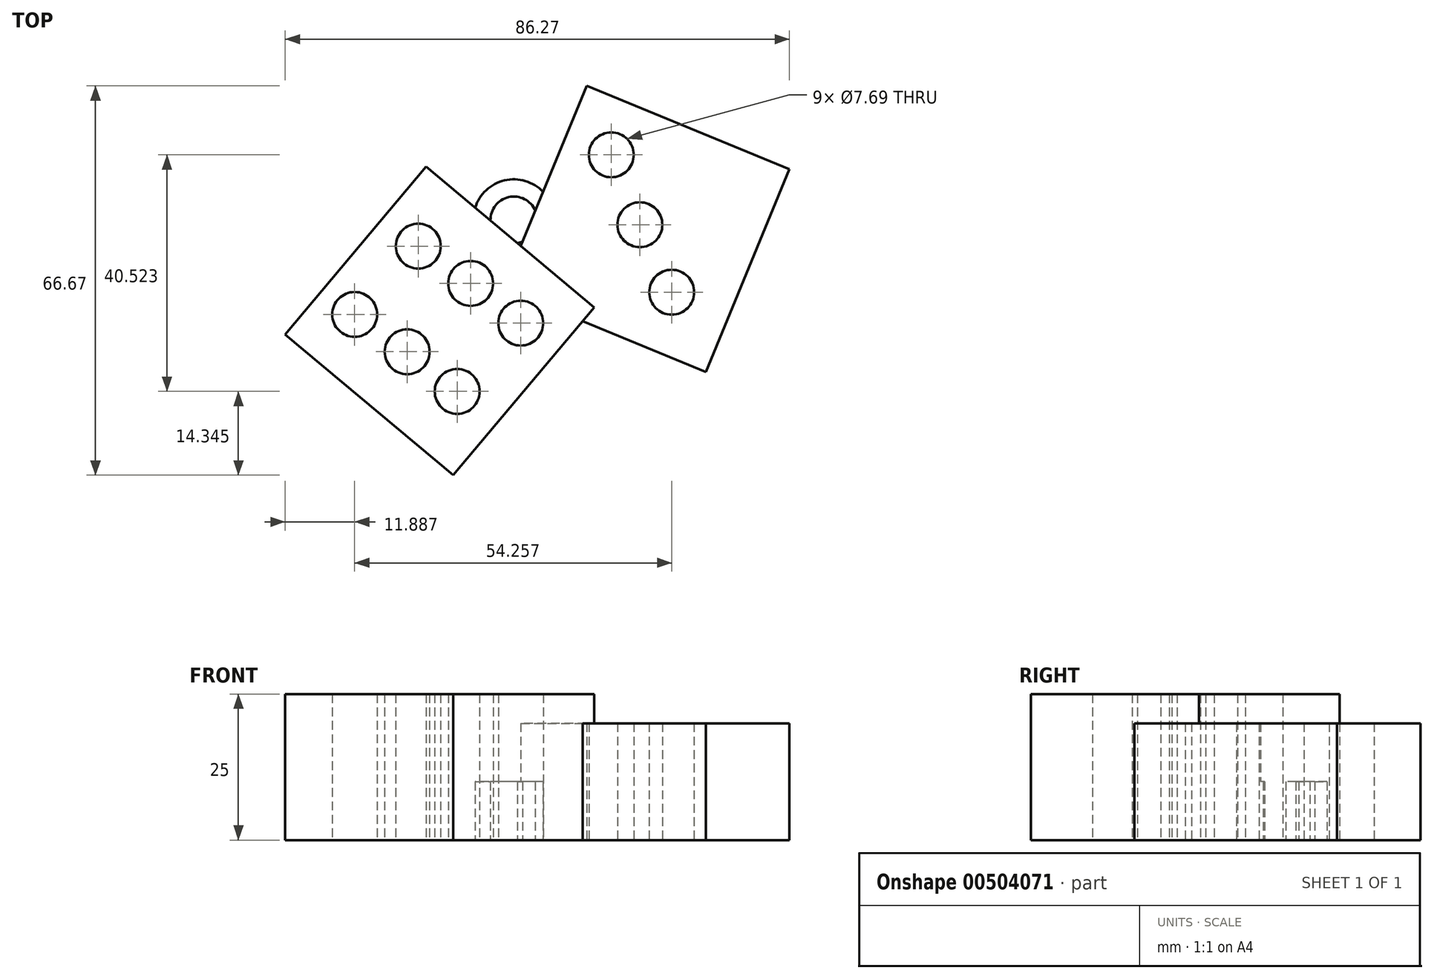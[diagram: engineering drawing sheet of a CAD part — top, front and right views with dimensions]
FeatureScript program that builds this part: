
annotation { "Feature Type Name" : "Feature", "Feature Type Description" : "" }
export const myFeature = defineFeature(function(context is Context, id is Id, definition is map)
    precondition{}
    {
        {
            var Q0;
            Q0=qCreatedBy(makeId("Top.planeOp"),FACE);
            var sketch = newSketch(context, id + "F0", { "sketchPlane" : qUnion([Q0])});
            skLineSegment(sketch, "E0.bottom", {"start": v(-13.76, 11) * mm, "end": v(14.98, -13.11) * mm});
            skLineSegment(sketch, "E0.top", {"start": v(-37.87, -17.74) * mm, "end": v(-9.13, -41.85) * mm});
            skLineSegment(sketch, "E0.left", {"start": v(-13.76, 11) * mm, "end": v(-37.87, -17.74) * mm});
            skLineSegment(sketch, "E0.right", {"start": v(14.98, -13.11) * mm, "end": v(-9.13, -41.85) * mm});
            skLineSegment(sketch, "E1.bottom", {"start": v(13.72, 24.82) * mm, "end": v(48.4, 10.53) * mm});
            skLineSegment(sketch, "E1.top", {"start": v(-0.57, -9.87) * mm, "end": v(34.11, -24.16) * mm});
            skLineSegment(sketch, "E1.left", {"start": v(13.72, 24.82) * mm, "end": v(-0.57, -9.87) * mm});
            skLineSegment(sketch, "E1.right", {"start": v(48.4, 10.53) * mm, "end": v(34.11, -24.16) * mm});
            skSolve(sketch);
        }
        {
            var Q0;
            {var subQ0=sQuery(id+"F0.wireOp",EDGE,"E0.right");var subQ1=sQuery(id+"F0.wireOp",EDGE,"E0.bottom");var subQ2=makeQuery(id+"F0.imprint","INTERSECT",VERTEX,{"derivedFrom":[subQ1,subQ0]});Q0=makeQuery(id+"F0.imprint","IMPRINT",FACE,{"disambiguationData":[TD([[makeQuery(id+"F0.imprint","IMPRINT",EDGE,{"disambiguationData":[TD([[subQ2,1.0]])],"derivedFrom":subQ1}),-1.0]])]});}
            var Q1;
            {var subQ1=sQuery(id+"F0.wireOp",EDGE,"E0.top");Q1=makeQuery(id+"F0.imprint","IMPRINT",FACE,{"disambiguationData":[TD([[makeQuery(id+"F0.imprint","IMPRINT",EDGE,{"derivedFrom":subQ1}),1.0]])]});}
            extrude(context, id + "F1", {"entities" : qUnion([Q0, Q1]), "depth" : 25 * mm});
        }
        {
            var Q0;
            {var subQ6=sQuery(id+"F0.wireOp",EDGE,"E1.bottom");Q0=makeQuery(id+"F0.imprint","IMPRINT",FACE,{"disambiguationData":[TD([[makeQuery(id+"F0.imprint","IMPRINT",EDGE,{"derivedFrom":subQ6}),-1.0]])]});}
            extrude(context, id + "F2", {"entities" : qUnion([Q0]), "operationType" : NewBodyOperationType.ADD, "depth" : 20 * mm});
        }
        {
            var Q0;
            Q0=qCreatedBy(makeId("Top.planeOp"),FACE);
            var sketch = newSketch(context, id + "F3", { "sketchPlane" : qUnion([Q0])});
            skCircle(sketch, "E2", {"center": v(-15.1, -2.62) * mm, "radius": 3.84 * mm});
            skCircle(sketch, "E3.1.0.0", {"center": v(-25.98, -14.32) * mm, "radius": 3.84 * mm});
            skCircle(sketch, "E4", {"center": v(-6.13, -9.01) * mm, "radius": 3.84 * mm});
            skCircle(sketch, "E5.1.0.0", {"center": v(-17, -20.7) * mm, "radius": 3.84 * mm});
            skCircle(sketch, "E6", {"center": v(2.44, -15.81) * mm, "radius": 3.84 * mm});
            skCircle(sketch, "E7.1.0.0", {"center": v(-8.44, -27.5) * mm, "radius": 3.84 * mm});
            skCircle(sketch, "E8", {"center": v(17.94, 13.02) * mm, "radius": 3.84 * mm});
            skCircle(sketch, "E9", {"center": v(22.83, 1.05) * mm, "radius": 3.84 * mm});
            skCircle(sketch, "E10", {"center": v(28.27, -10.5) * mm, "radius": 3.84 * mm});
            skSolve(sketch);
        }
        {
            var Q0;
            Q0 = qSketchRegion(id + "F3", true);
            extrude(context, id + "F4", {"entities" : qUnion([Q0]), "operationType" : NewBodyOperationType.REMOVE, "depth" : 25 * mm});
        }
        {
            var Q0;
            Q0=qCreatedBy(makeId("Top.planeOp"),FACE);
            var sketch = newSketch(context, id + "F5", { "sketchPlane" : qUnion([Q0])});
            skCircle(sketch, "E11", {"center": v(1.26, 1.87) * mm, "radius": 6.95 * mm});
            skCircle(sketch, "E12", {"center": v(1.26, 1.87) * mm, "radius": 4 * mm});
            skSolve(sketch);
        }
        {
            var Q0;
            Q0 = qSketchRegion(id + "F5", true);
            extrude(context, id + "F6", {"entities" : qUnion([Q0]), "operationType" : NewBodyOperationType.ADD, "depth" : 10 * mm});
        }
    });
